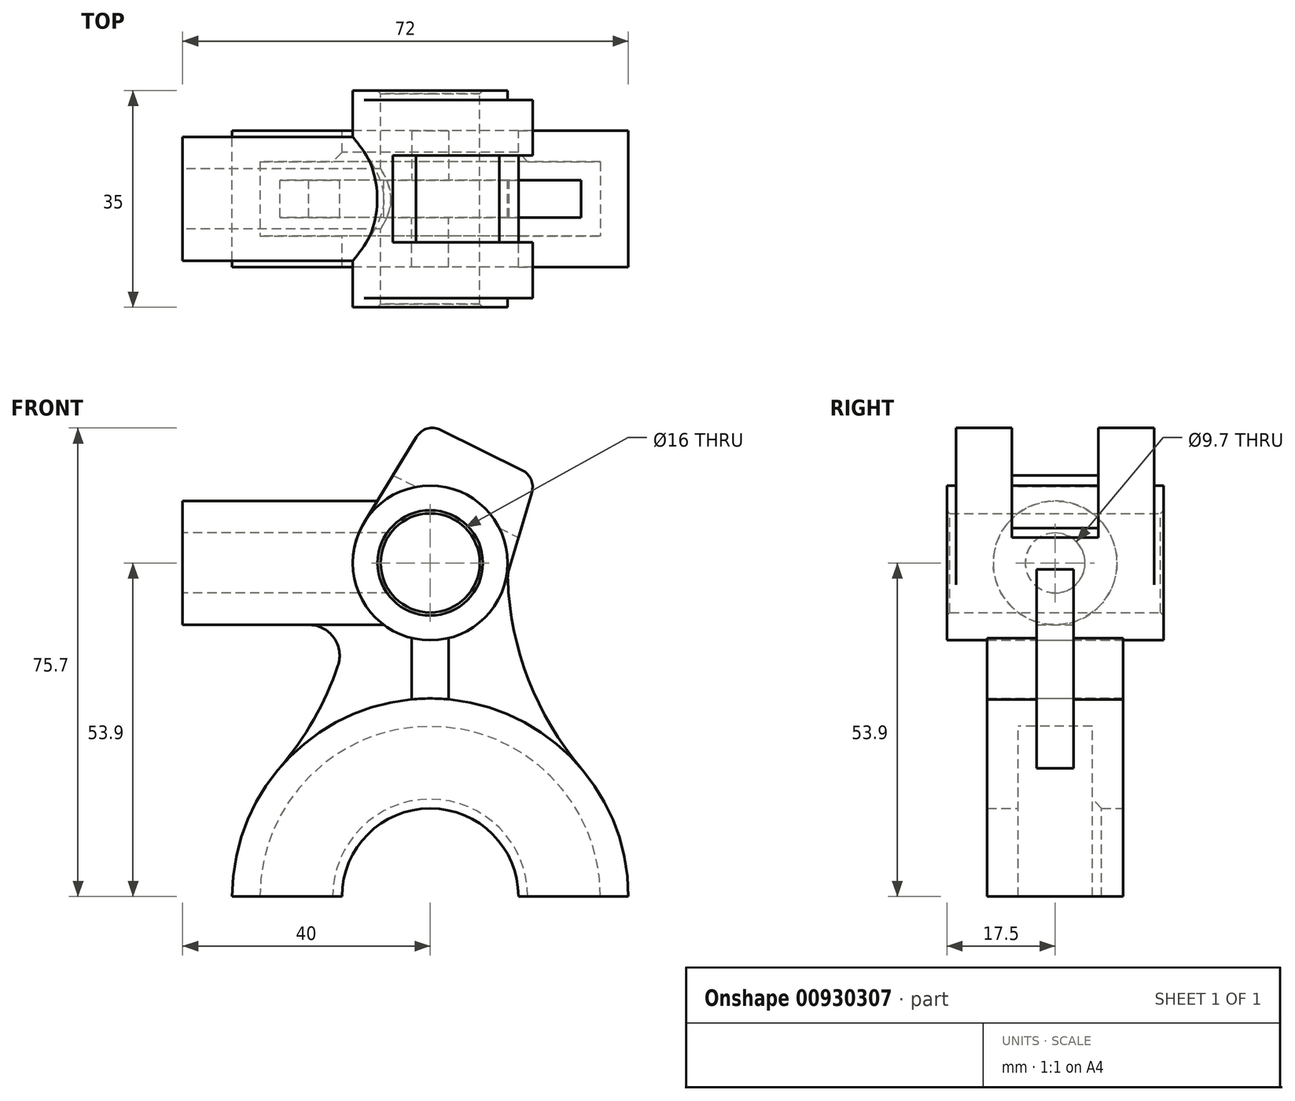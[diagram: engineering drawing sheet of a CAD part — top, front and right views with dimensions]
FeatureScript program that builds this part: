
annotation { "Feature Type Name" : "Feature", "Feature Type Description" : "" }
export const myFeature = defineFeature(function(context is Context, id is Id, definition is map)
    precondition{}
    {
        {
            var Q0;
            Q0=qCreatedBy(makeId("Front.planeOp"),FACE);
            var sketch = newSketch(context, id + "F0", { "sketchPlane" : qUnion([Q0])});
            skArc(sketch, "E0", {"start": v(14.25, 2) * mm, "mid": v(0, 16.25) * mm, "end": v(-14.25, 2) * mm});
            skArc(sketch, "E1", {"start": v(32, 2) * mm, "mid": v(0, 34) * mm, "end": v(-32, 2) * mm});
            skLineSegment(sketch, "E2", {"start": v(-32, 2) * mm, "end": v(-14.25, 2) * mm});
            skLineSegment(sketch, "E3.trimOffspring", {"start": v(14.25, 2) * mm, "end": v(32, 2) * mm});
            skArc(sketch, "E4", {"start": v(27.5, 2) * mm, "mid": v(0, 29.5) * mm, "end": v(-27.5, 2) * mm});
            skCircle(sketch, "E5", {"center": v(0, 55.9) * mm, "radius": 12.5 * mm});
            skCircle(sketch, "E6", {"center": v(0, 55.9) * mm, "radius": 8 * mm});
            skSolve(sketch);
        }
        {
            var Q0;
            {var subQ0=sQuery(id+"F0.wireOp",EDGE,"E1");Q0=makeQuery(id+"F0.imprint","IMPRINT",FACE,{"disambiguationData":[TD([[makeQuery(id+"F0.imprint","IMPRINT",EDGE,{"derivedFrom":subQ0}),1.0]])]});}
            var Q1;
            {var subQ0=sQuery(id+"F0.wireOp",EDGE,"E0");Q1=makeQuery(id+"F0.imprint","IMPRINT",FACE,{"disambiguationData":[TD([[makeQuery(id+"F0.imprint","IMPRINT",EDGE,{"derivedFrom":subQ0}),-1.0]])]});}
            extrude(context, id + "F1", {"entities" : qUnion([Q0, Q1]), "depth" : 11 * mm, "offsetDistance" : 25 * mm, "hasSecondDirection" : true, "secondDirectionOppositeDirection" : true, "secondDirectionDepth" : 11 * mm});
        }
        {
            var Q0;
            {var subQ0=sQuery(id+"F0.wireOp",EDGE,"E0");Q0=makeQuery(id+"F0.imprint","IMPRINT",FACE,{"disambiguationData":[TD([[makeQuery(id+"F0.imprint","IMPRINT",EDGE,{"derivedFrom":subQ0}),-1.0]])]});}
            extrude(context, id + "F2", {"entities" : qUnion([Q0]), "operationType" : NewBodyOperationType.REMOVE, "oppositeDirection" : true, "depth" : 6 * mm, "offsetDistance" : 25 * mm, "hasSecondDirection" : true, "secondDirectionOppositeDirection" : false, "secondDirectionDepth" : 6 * mm});
        }
        {
            var Q0;
            Q0=makeQuery(id+"F2.boolean.opBoolean","COPY",EDGE,{"derivedFrom":makeQuery(id+"F2.opExtrude","CAP_EDGE",EDGE,{"disambiguationData":[OSD([sQuery(id+"F0.wireOp",EDGE,"E0")])],"isStart":true})});
            var Q1;
            Q1=makeQuery(id+"F2.boolean.opBoolean","COPY",EDGE,{"derivedFrom":makeQuery(id+"F2.opExtrude","CAP_EDGE",EDGE,{"disambiguationData":[OSD([sQuery(id+"F0.wireOp",EDGE,"E0")])],"isStart":false})});
            chamfer(context, id + "F3", {"entities" : qUnion([Q0, Q1]), "width" : 1.5 * mm, "tangentPropagation" : true});
        }
        {
            var Q0;
            Q0=makeQuery(id+"F0.imprint","IMPRINT",FACE,{"disambiguationData":[TD([[makeQuery(id+"F0.imprint","IMPRINT",EDGE,{"derivedFrom":sQuery(id+"F0.wireOp",EDGE,"E5")}),1.0]])]});
            extrude(context, id + "F4", {"entities" : qUnion([Q0]), "depth" : 17.5 * mm, "offsetDistance" : 25 * mm, "hasSecondDirection" : true, "secondDirectionOppositeDirection" : true, "secondDirectionDepth" : 17.5 * mm});
        }
        {
            var Q0;
            Q0=makeQuery(id+"F4.opExtrude","CAP_EDGE",EDGE,{"disambiguationData":[OSD([sQuery(id+"F0.wireOp",EDGE,"E6")])],"isStart":false});
            var Q1;
            Q1=makeQuery(id+"F4.opExtrude","CAP_EDGE",EDGE,{"disambiguationData":[OSD([sQuery(id+"F0.wireOp",EDGE,"E6")])],"isStart":true});
            chamfer(context, id + "F5", {"entities" : qUnion([Q0, Q1]), "width" : 0.5 * mm, "tangentPropagation" : true});
        }
        {
            var Q0;
            Q0=qCreatedBy(makeId("Right.planeOp"),FACE);
            cPlane(context, id + "F6", {"entities" : qUnion([Q0]), "cplaneType" : CPlaneType.OFFSET, "offset" : 40 * mm, "oppositeDirection" : true, "width" : 150 * mm, "height" : 150 * mm});
        }
        {
            var Q0;
            Q0=qCreatedBy(id+"F6.planeOp",FACE);
            var sketch = newSketch(context, id + "F7", { "sketchPlane" : qUnion([Q0])});
            skCircle(sketch, "E7", {"center": v(0, 55.9) * mm, "radius": 10 * mm});
            skCircle(sketch, "E8", {"center": v(0, 55.9) * mm, "radius": 4.85 * mm});
            skSolve(sketch);
        }
        {
            var Q0;
            Q0=makeQuery(id+"F7.imprint","IMPRINT",FACE,{"disambiguationData":[TD([[makeQuery(id+"F7.imprint","IMPRINT",EDGE,{"derivedFrom":sQuery(id+"F7.wireOp",EDGE,"E7")}),1.0]])]});
            var Q1;
            Q1=makeQuery(id+"F4.opExtrude","SWEPT_FACE",FACE,{"disambiguationData":[OSD([sQuery(id+"F0.wireOp",EDGE,"E5")])]});
            extrude(context, id + "F8", {"entities" : qUnion([Q0]), "operationType" : NewBodyOperationType.ADD, "endBound" : BoundingType.UP_TO_SURFACE, "depth" : 25 * mm, "endBoundEntityFace" : qUnion([Q1]), "offsetDistance" : 25 * mm});
        }
        {
            var Q0;
            Q0=makeQuery(id+"F7.imprint","IMPRINT",FACE,{"disambiguationData":[TD([[makeQuery(id+"F7.imprint","IMPRINT",EDGE,{"derivedFrom":sQuery(id+"F7.wireOp",EDGE,"E8")}),1.0]])]});
            var Q1;
            Q1=makeQuery(id+"F4.opExtrude","SWEPT_FACE",FACE,{"disambiguationData":[OSD([sQuery(id+"F0.wireOp",EDGE,"E6")])]});
            extrude(context, id + "F9", {"entities" : qUnion([Q0]), "operationType" : NewBodyOperationType.REMOVE, "endBound" : BoundingType.UP_TO_SURFACE, "depth" : 25 * mm, "endBoundEntityFace" : qUnion([Q1]), "offsetDistance" : 25 * mm});
        }
        {
            var Q0;
            Q0=qCreatedBy(makeId("Front.planeOp"),FACE);
            var sketch = newSketch(context, id + "F10", { "sketchPlane" : qUnion([Q0])});
            skLineSegment(sketch, "E9", {"start": v(0, 55.9) * mm, "end": v(31.62, 40.24) * mm});
            skLineSegment(sketch, "E10.0", {"start": v(1.67, 77.4) * mm, "end": v(14.87, 70.86) * mm});
            skLineSegment(sketch, "E11", {"start": v(11.99, 52.35) * mm, "end": v(16.41, 67.32) * mm});
            skLineSegment(sketch, "E12", {"start": v(-10.8, 62.2) * mm, "end": v(-2.22, 76.26) * mm});
            skPoint(sketch, "E13.visualSharp", {"position": v(-0.8, 78.61) * mm});
            skArc(sketch, "E13.filletArc", {"start": v(1.67, 77.4) * mm, "mid": v(-0.5, 77.58) * mm, "end": v(-2.22, 76.26) * mm});
            skPoint(sketch, "E14.visualSharp", {"position": v(17.13, 69.74) * mm});
            skArc(sketch, "E14.filletArc", {"start": v(16.41, 67.32) * mm, "mid": v(16.29, 69.37) * mm, "end": v(14.87, 70.86) * mm});
            skArc(sketch, "E15.0", {"start": v(11.99, 52.35) * mm, "mid": v(5.07, 67.33) * mm, "end": v(-10.67, 62.4) * mm});
            skLineSegment(sketch, "E16.0", {"start": v(-6.02, 70.04) * mm, "end": v(14.25, 60) * mm});
            skSolve(sketch);
        }
        {
            var Q0;
            Q0=makeQuery(id+"F10.imprint","IMPRINT",FACE,{"disambiguationData":[TD([[makeQuery(id+"F10.imprint","IMPRINT",EDGE,{"derivedFrom":sQuery(id+"F10.wireOp",EDGE,"E10.0")}),-1.0]])]});
            var Q1;
            {var subQ0=sQuery(id+"F10.wireOp",EDGE,"E15.0");var subQ1=sQuery(id+"F10.wireOp",EDGE,"E11");var subQ2=makeQuery(id+"F10.imprint","INTERSECT",VERTEX,{"derivedFrom":[subQ1,subQ0]});Q1=makeQuery(id+"F10.imprint","IMPRINT",FACE,{"disambiguationData":[TD([[makeQuery(id+"F10.imprint","IMPRINT",EDGE,{"disambiguationData":[TD([[subQ2,-1.0]])],"derivedFrom":subQ1}),1.0]])]});}
            var Q2;
            {var subQ0=sQuery(id+"F10.wireOp",EDGE,"E15.0");var subQ1=sQuery(id+"F10.wireOp",EDGE,"E12");var subQ2=makeQuery(id+"F10.imprint","INTERSECT",VERTEX,{"derivedFrom":[subQ1,subQ0]});Q2=makeQuery(id+"F10.imprint","IMPRINT",FACE,{"disambiguationData":[TD([[makeQuery(id+"F10.imprint","IMPRINT",EDGE,{"disambiguationData":[TD([[subQ2,-1.0]])],"derivedFrom":subQ1}),-1.0]])]});}
            extrude(context, id + "F11", {"entities" : qUnion([Q0, Q1, Q2]), "operationType" : NewBodyOperationType.ADD, "depth" : 16 * mm, "offsetDistance" : 25 * mm, "hasSecondDirection" : true, "secondDirectionOppositeDirection" : true, "secondDirectionDepth" : 16 * mm});
        }
        {
            var Q0;
            {var subQ0=sQuery(id+"F10.wireOp",EDGE,"E16.0");var subQ1=sQuery(id+"F10.wireOp",EDGE,"E15.0");var subQ2=makeQuery(id+"F10.imprint","INTERSECT",VERTEX,{"disambiguationData":[OD(0.0)],"derivedFrom":[subQ1,subQ0]});Q0=makeQuery(id+"F10.imprint","IMPRINT",FACE,{"disambiguationData":[TD([[makeQuery(id+"F10.imprint","IMPRINT",EDGE,{"disambiguationData":[TD([[subQ2,-1.0]])],"derivedFrom":subQ1}),1.0]])]});}
            var Q1;
            Q1=makeQuery(id+"F10.imprint","IMPRINT",FACE,{"disambiguationData":[TD([[makeQuery(id+"F10.imprint","IMPRINT",EDGE,{"derivedFrom":sQuery(id+"F10.wireOp",EDGE,"E10.0")}),-1.0]])]});
            extrude(context, id + "F12", {"entities" : qUnion([Q0, Q1]), "operationType" : NewBodyOperationType.REMOVE, "oppositeDirection" : true, "depth" : 7 * mm, "offsetDistance" : 25 * mm, "hasSecondDirection" : true, "secondDirectionOppositeDirection" : false, "secondDirectionDepth" : 7 * mm});
        }
        {
            var Q0;
            Q0=qCreatedBy(makeId("Front.planeOp"),FACE);
            var sketch = newSketch(context, id + "F13", { "sketchPlane" : qUnion([Q0])});
            skArc(sketch, "E17", {"start": v(12.53, 53.27) * mm, "mid": v(15.88, 37) * mm, "end": v(24.39, 22.72) * mm});
            skArc(sketch, "E18.0", {"start": v(32, 2) * mm, "mid": v(0, 34) * mm, "end": v(-32, 2) * mm});
            skCircle(sketch, "E18.1", {"center": v(0, 55.9) * mm, "radius": 12.5 * mm});
            skLineSegment(sketch, "E19.0", {"start": v(12.73, 54.87) * mm, "end": v(16.41, 67.32) * mm});
            skArc(sketch, "E20", {"start": v(-24.3, 22.83) * mm, "mid": v(-18.81, 30.61) * mm, "end": v(-14.9, 39.3) * mm});
            skLineSegment(sketch, "E21", {"start": v(-19.64, 45.9) * mm, "end": v(-40, 45.9) * mm});
            skArc(sketch, "E22.filletArc", {"start": v(-14.9, 39.3) * mm, "mid": v(-15.58, 43.81) * mm, "end": v(-19.64, 45.9) * mm});
            skLineSegment(sketch, "E23", {"start": v(-7.5, 45.9) * mm, "end": v(-40, 45.9) * mm});
            skPoint(sketch, "E24.newPointB", {"position": v(11.99, 52.35) * mm});
            skArc(sketch, "E24.filletArc", {"start": v(12.73, 54.87) * mm, "mid": v(12.56, 54.08) * mm, "end": v(12.53, 53.27) * mm});
            skLineSegment(sketch, "E25.0", {"start": v(11.99, 52.35) * mm, "end": v(16.41, 67.32) * mm});
            skSolve(sketch);
        }
        {
            var Q0;
            {var subQ1=sQuery(id+"F13.wireOp",EDGE,"E17");Q0=makeQuery(id+"F13.imprint","IMPRINT",FACE,{"disambiguationData":[TD([[makeQuery(id+"F13.imprint","IMPRINT",EDGE,{"derivedFrom":subQ1}),-1.0]])]});}
            extrude(context, id + "F14", {"entities" : qUnion([Q0]), "depth" : 3 * mm, "offsetDistance" : 25 * mm, "hasSecondDirection" : true, "secondDirectionOppositeDirection" : true, "secondDirectionDepth" : 3 * mm});
        }
        {
            var Q0;
            Q0=makeQuery(id+"F14.opExtrude","CAP_FACE",FACE,{"disambiguationData":[OSD([sQuery(id+"F13.wireOp",EDGE,"E17"),sQuery(id+"F13.wireOp",EDGE,"E18.0"),sQuery(id+"F13.wireOp",EDGE,"E18.1"),sQuery(id+"F13.wireOp",EDGE,"E20"),sQuery(id+"F13.wireOp",EDGE,"E22.filletArc"),sQuery(id+"F13.wireOp",EDGE,"E23"),sQuery(id+"F13.wireOp",EDGE,"E24.filletArc"),sQuery(id+"F13.wireOp",EDGE,"E25.0")])],"isStart":false});
            var sketch = newSketch(context, id + "F15", { "sketchPlane" : qUnion([Q0])});
            skLineSegment(sketch, "E26", {"start": v(-3, 43.77) * mm, "end": v(-3, 33.86) * mm});
            skLineSegment(sketch, "E27", {"start": v(3, 43.77) * mm, "end": v(3, 33.86) * mm});
            skCircle(sketch, "E28.0", {"center": v(0, 55.9) * mm, "radius": 12.5 * mm});
            skArc(sketch, "E29.0", {"start": v(32, 2) * mm, "mid": v(0, 34) * mm, "end": v(-32, 2) * mm});
            skSolve(sketch);
        }
        {
            var Q0;
            {var subQ0=sQuery(id+"F15.wireOp",EDGE,"E26");Q0=makeQuery(id+"F15.imprint","IMPRINT",FACE,{"disambiguationData":[TD([[makeQuery(id+"F15.imprint","IMPRINT",EDGE,{"derivedFrom":subQ0}),1.0]])]});}
            var Q1;
            Q1=makeQuery(id+"F1.opExtrude","CAP_FACE",FACE,{"disambiguationData":[OSD([sQuery(id+"F0.wireOp",EDGE,"E0"),sQuery(id+"F0.wireOp",EDGE,"E1"),sQuery(id+"F0.wireOp",EDGE,"E2"),sQuery(id+"F0.wireOp",EDGE,"E3.trimOffspring")])],"isStart":false});
            extrude(context, id + "F16", {"entities" : qUnion([Q0]), "endBound" : BoundingType.UP_TO_SURFACE, "depth" : 25 * mm, "endBoundEntityFace" : qUnion([Q1]), "offsetDistance" : 25 * mm});
        }
        {
            var Q0;
            Q0=makeQuery(id+"F16.opExtrude","SWEPT_BODY",BODY,{"disambiguationData":[OSD([sQuery(id+"F15.wireOp",EDGE,"E26"),sQuery(id+"F15.wireOp",EDGE,"E27"),sQuery(id+"F15.wireOp",EDGE,"E28.0"),sQuery(id+"F15.wireOp",EDGE,"E29.0")])]});
            var Q1;
            Q1=qCreatedBy(makeId("Front.planeOp"),FACE);
            mirror(context, id + "F17", {"entities" : qUnion([Q0]), "mirrorPlane" : qUnion([Q1])});
        }
    });
